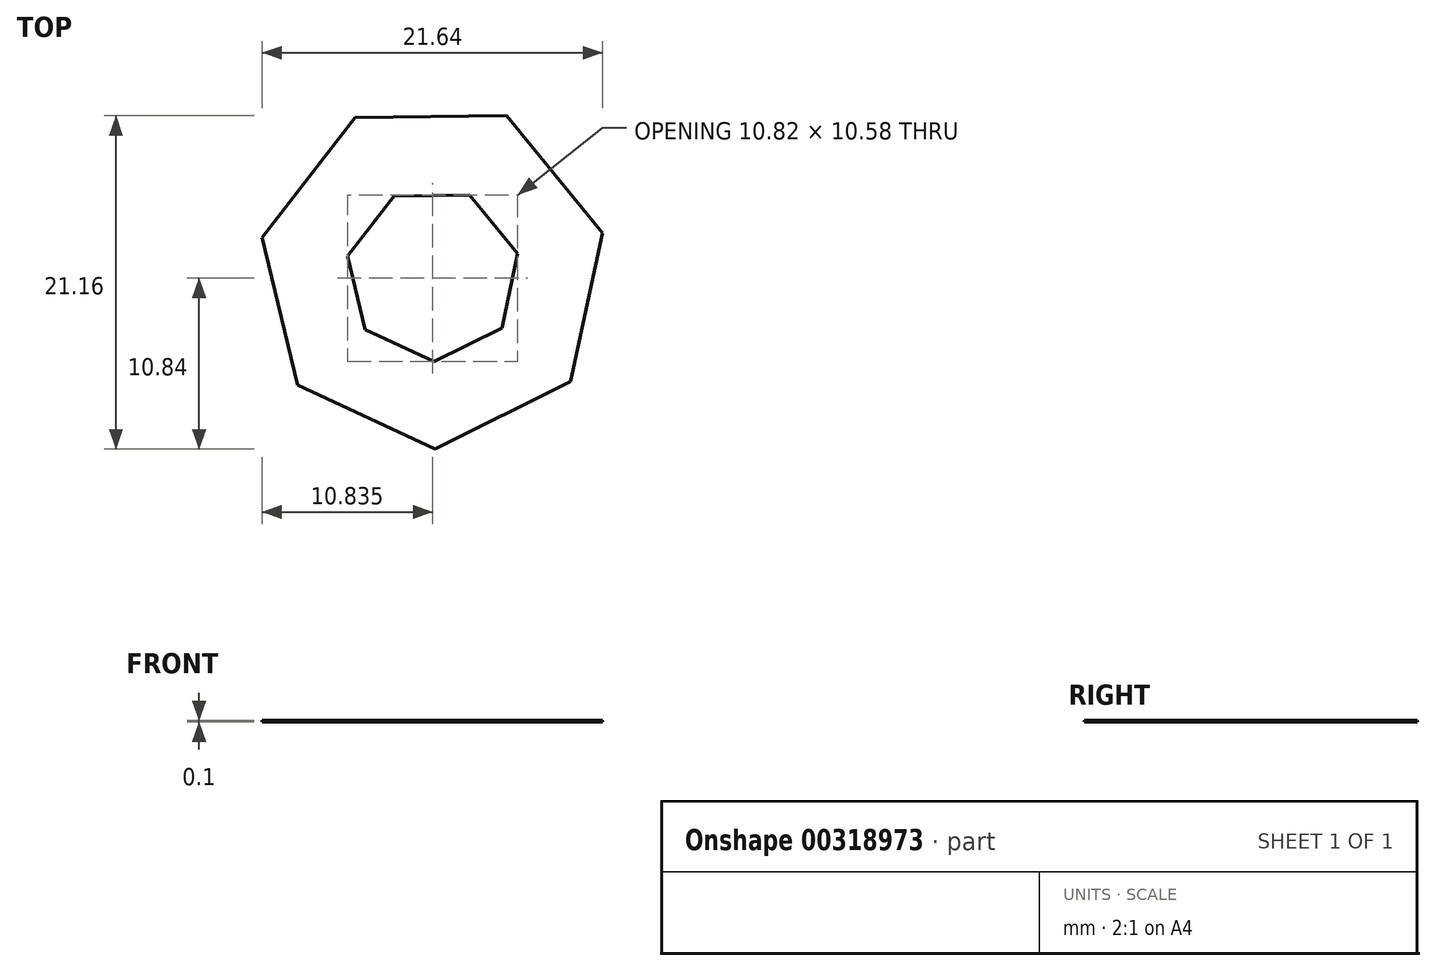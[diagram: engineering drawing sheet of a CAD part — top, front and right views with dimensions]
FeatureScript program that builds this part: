
annotation { "Feature Type Name" : "Feature", "Feature Type Description" : "" }
export const myFeature = defineFeature(function(context is Context, id is Id, definition is map)
    precondition{}
    {
        {
            var Q0;
            Q0=qCreatedBy(makeId("Top.planeOp"),FACE);
            var sketch = newSketch(context, id + "F0", { "sketchPlane" : qUnion([Q0])});
            skCircle(sketch, "E0.cCircle", {"center": v(0, 0) * mm, "radius": 11.1 * mm, "construction": true});
            skLineSegment(sketch, "E0.0", {"start": v(-4.94, 9.94) * mm, "end": v(4.7, 10.06) * mm});
            skLineSegment(sketch, "E0.1", {"start": v(4.7, 10.06) * mm, "end": v(10.79, 2.6) * mm});
            skLineSegment(sketch, "E0.2", {"start": v(10.79, 2.6) * mm, "end": v(8.76, -6.81) * mm});
            skLineSegment(sketch, "E0.3", {"start": v(8.76, -6.81) * mm, "end": v(0.14, -11.1) * mm});
            skLineSegment(sketch, "E0.4", {"start": v(0.14, -11.1) * mm, "end": v(-8.6, -7.03) * mm});
            skLineSegment(sketch, "E0.5", {"start": v(-8.6, -7.03) * mm, "end": v(-10.85, 2.33) * mm});
            skLineSegment(sketch, "E0.6", {"start": v(-10.85, 2.33) * mm, "end": v(-4.94, 9.94) * mm});
            skLineSegment(sketch, "E1.0", {"start": v(-4.3, -3.51) * mm, "end": v(-5.43, 1.17) * mm});
            skLineSegment(sketch, "E1.1", {"start": v(0.07, -5.55) * mm, "end": v(-4.3, -3.51) * mm});
            skLineSegment(sketch, "E1.2", {"start": v(-2.47, 4.97) * mm, "end": v(2.35, 5.03) * mm});
            skLineSegment(sketch, "E1.3", {"start": v(2.35, 5.03) * mm, "end": v(5.4, 1.3) * mm});
            skLineSegment(sketch, "E1.4", {"start": v(5.4, 1.3) * mm, "end": v(4.38, -3.4) * mm});
            skLineSegment(sketch, "E1.5", {"start": v(-5.43, 1.17) * mm, "end": v(-2.47, 4.97) * mm});
            skLineSegment(sketch, "E1.6", {"start": v(4.38, -3.4) * mm, "end": v(0.07, -5.55) * mm});
            skSolve(sketch);
        }
        {
            var Q0;
            Q0=makeQuery(id+"F0.imprint","IMPRINT",FACE,{"disambiguationData":[TD([[makeQuery(id+"F0.imprint","IMPRINT",EDGE,{"derivedFrom":sQuery(id+"F0.wireOp",EDGE,"E0.0")}),-1.0]])]});
            extrude(context, id + "F1", {"entities" : qUnion([Q0]), "depth" : 0.1 * mm});
        }
    });
